# Revit family: 202_PRR-_-G-_+NK-SWA
name_source: partatom
category: Air Terminals
units: mm (PartAtom-declared; Revit-internal decimal feet)

## family parameters
Always vertical = Yes
Cut with Voids When Loaded = No
Part Type = Normal
Room Calculation Point = Yes
Round Connector Dimension = Use Diameter
Shared = No
Work Plane-Based = No

## types (5) — shared parameters
CAT0 = Yes
CL_Location_5000 = 5000 mm  [stored 16.4042 ft]
DZ = 5 mm  [stored 0.0164042 ft]
Description = EXPANSION BOXES TO BE MOUNTED UNDER THE NK-SWA DIFFUSERS
L_ARR = 400 mm  [stored 1.31234 ft]
Manufacturer = Alnor
QmdConnectorList = 201;D
SW1 = No
SW10 = No
SW2 = Yes
URL = http://www.ventilation-alnor.co.uk
W_ARR = 400 mm  [stored 1.31234 ft]
XRefLineVPlnId = 7453
YRefLineVPlnId = 7456
magiPartTypeId = 202
magiProductFamilyId = PRR-*-G-*+NK-SWA
zero-valued in all types: CLBTZ, H_ARR

## per-type parameters (varying)
| type | A2 | C1 | D | DPX | DPZ | DS | R | XX | magiProductId |
| NK-SWA-300+PRR-G-160 | 298 mm | 250 mm  [stored 0.82021 ft] | 160 mm | 127 mm  [stored 0.416667 ft] | 125 mm  [stored 0.410105 ft] | 254 mm  [stored 0.833333 ft] | 80 mm  [stored 0.262467 ft] | 25 mm  [stored 0.082021 ft] | PRR-300-G-160+NK-SWA |
| NK-SWA-625+PRR-G-250 | 313 mm | 350 mm | 250 mm | 265 mm | 175 mm | 530 mm | 125 mm  [stored 0.410105 ft] | 53 mm | PRR-625-G-250+NK-SWA |
| NK-SWA-595+PRR-G-250 | 298 mm | 350 mm | 250 mm | 265 mm | 175 mm | 530 mm | 125 mm  [stored 0.410105 ft] | 53 mm | PRR-595-G-250+NK-SWA |
| NK-SWA-500+PRR-G-200 | 298 mm | 300 mm | 200 mm | 220 mm | 150 mm | 440 mm | 100 mm  [stored 0.328084 ft] | 44 mm | PRR-500-G-200+NK-SWA |
| NK-SWA-400+PRR-G-200 | 298 mm | 250 mm  [stored 0.82021 ft] | 200 mm | 168 mm | 125 mm  [stored 0.410105 ft] | 336 mm  [stored 1.10236 ft] | 100 mm  [stored 0.328084 ft] | 34 mm | PRR-400-G-200+NK-SWA |

note: column(s) folded — value = type name in every type: MC Product Code

note: [stored X ft] marks values corroborated as IEEE doubles in the binary element streams (Revit-internal decimal feet)

## geometry (parser evidence)
native form markers: Blend x2, Sweep x2
no freeform markers — native parametric forms only
